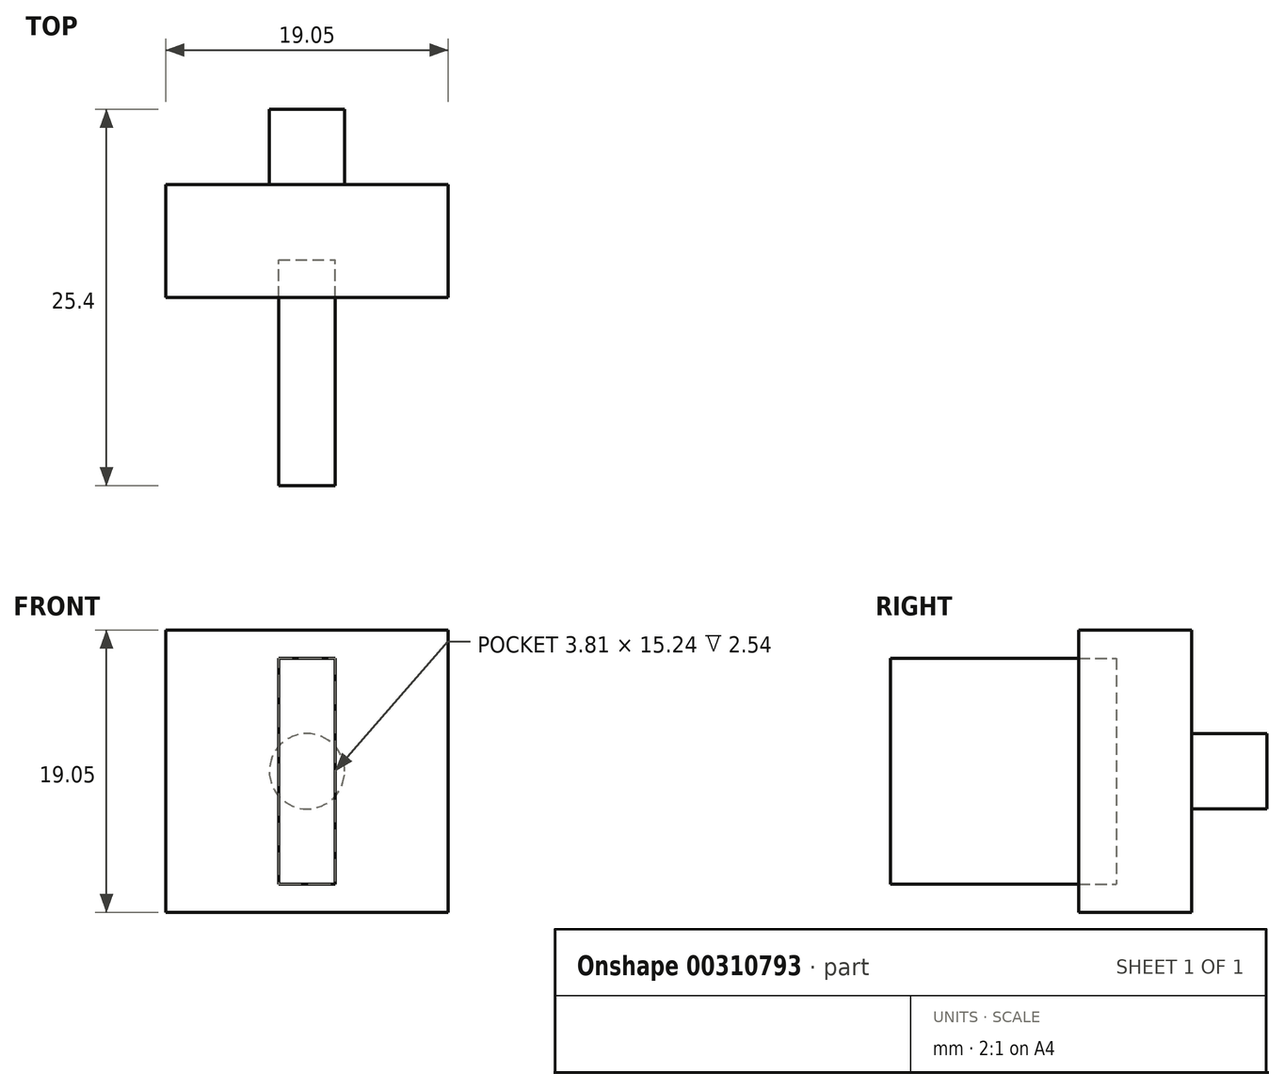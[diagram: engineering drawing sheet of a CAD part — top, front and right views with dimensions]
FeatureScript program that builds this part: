
annotation { "Feature Type Name" : "Feature", "Feature Type Description" : "" }
export const myFeature = defineFeature(function(context is Context, id is Id, definition is map)
    precondition{}
    {
        {
            var Q0;
            Q0=qCreatedBy(makeId("Front.planeOp"),FACE);
            var sketch = newSketch(context, id + "F0", { "sketchPlane" : qUnion([Q0])});
            skLineSegment(sketch, "E0", {"start": v(-7.62, 0) * mm, "end": v(11.43, 0) * mm});
            skLineSegment(sketch, "E1", {"start": v(11.43, 0) * mm, "end": v(11.43, 19.05) * mm});
            skLineSegment(sketch, "E2", {"start": v(11.43, 19.05) * mm, "end": v(-7.62, 19.05) * mm});
            skLineSegment(sketch, "E3", {"start": v(-7.62, 19.05) * mm, "end": v(-7.62, 0) * mm});
            skSolve(sketch);
        }
        {
            var Q0;
            Q0=makeQuery(id+"F0.imprint","IMPRINT",FACE,{"disambiguationData":[TD([[makeQuery(id+"F0.imprint","IMPRINT",EDGE,{"derivedFrom":sQuery(id+"F0.wireOp",EDGE,"E0")}),1.0]])]});
            extrude(context, id + "F1", {"entities" : qUnion([Q0]), "depth" : 7.62 * mm});
        }
        {
            var Q0;
            Q0=makeQuery(id+"F1.opExtrude","CAP_FACE",FACE,{"disambiguationData":[OSD([sQuery(id+"F0.wireOp",EDGE,"E0"),sQuery(id+"F0.wireOp",EDGE,"E1"),sQuery(id+"F0.wireOp",EDGE,"E2"),sQuery(id+"F0.wireOp",EDGE,"E3")])],"isStart":false});
            var sketch = newSketch(context, id + "F2", { "sketchPlane" : qUnion([Q0])});
            skLineSegment(sketch, "E4", {"start": v(0, 1.9) * mm, "end": v(3.8, 1.9) * mm});
            skLineSegment(sketch, "E5", {"start": v(3.8, 1.9) * mm, "end": v(3.8, 17.14) * mm});
            skLineSegment(sketch, "E6", {"start": v(3.8, 17.14) * mm, "end": v(0, 17.14) * mm});
            skLineSegment(sketch, "E7", {"start": v(0, 17.14) * mm, "end": v(0, 1.9) * mm});
            skSolve(sketch);
        }
        {
            var Q0;
            Q0=makeQuery(id+"F2.imprint","IMPRINT",FACE,{"disambiguationData":[TD([[makeQuery(id+"F2.imprint","IMPRINT",EDGE,{"derivedFrom":sQuery(id+"F2.wireOp",EDGE,"cbMtKTGd-g65i-xnvt-AXoW-RrOancOfgppl")}),1.0]])]});
            var Q1;
            Q1=makeQuery(id+"F2.imprint","IMPRINT",FACE,{"disambiguationData":[TD([[makeQuery(id+"F2.imprint","IMPRINT",EDGE,{"derivedFrom":sQuery(id+"F2.wireOp",EDGE,"E4")}),1.0]])]});
            extrude(context, id + "F3", {"entities" : qUnion([Q0, Q1]), "operationType" : NewBodyOperationType.REMOVE, "oppositeDirection" : true, "depth" : 2.54 * mm});
        }
        {
            var Q0;
            Q0=makeQuery(id+"F1.opExtrude","CAP_FACE",FACE,{"disambiguationData":[OSD([sQuery(id+"F0.wireOp",EDGE,"E0"),sQuery(id+"F0.wireOp",EDGE,"E1"),sQuery(id+"F0.wireOp",EDGE,"E2"),sQuery(id+"F0.wireOp",EDGE,"E3")])],"isStart":true});
            var sketch = newSketch(context, id + "F4", { "sketchPlane" : qUnion([Q0])});
            skPoint(sketch, "E8.centerSnap0", {"position": v(-11.43, 9.53) * mm});
            skCircle(sketch, "E9", {"center": v(-1.9, 9.53) * mm, "radius": 2.54 * mm});
            skPoint(sketch, "E9.centerSnap0", {"position": v(-1.9, 19.05) * mm});
            skPoint(sketch, "E9.centerSnap1", {"position": v(7.62, 9.53) * mm});
            skSolve(sketch);
        }
        {
            var Q0;
            Q0=makeQuery(id+"F4.imprint","IMPRINT",FACE,{"disambiguationData":[TD([[makeQuery(id+"F4.imprint","IMPRINT",EDGE,{"derivedFrom":sQuery(id+"F4.wireOp",EDGE,"E8")}),1.0]])]});
            var Q1;
            Q1=makeQuery(id+"F4.imprint","IMPRINT",FACE,{"disambiguationData":[TD([[makeQuery(id+"F4.imprint","IMPRINT",EDGE,{"derivedFrom":sQuery(id+"F4.wireOp",EDGE,"E9")}),1.0]])]});
            extrude(context, id + "F5", {"entities" : qUnion([Q0, Q1]), "operationType" : NewBodyOperationType.ADD, "depth" : 5.08 * mm});
        }
        {
            var Q0;
            Q0=makeQuery(id+"F3.boolean.opBoolean","COPY",FACE,{"derivedFrom":makeQuery(id+"F3.opExtrude","CAP_FACE",FACE,{"disambiguationData":[OSD([sQuery(id+"F2.wireOp",EDGE,"cbMtKTGd-g65i-xnvt-AXoW-RrOancOfgppl"),sQuery(id+"F2.wireOp",EDGE,"NMXBmVgW-MpaY-MJWR-DT77-MaYLcQVVOFlb"),sQuery(id+"F2.wireOp",EDGE,"Pu10IA7c-zYZb-xNST-tOOe-hBLO1BOZIXoM"),sQuery(id+"F2.wireOp",EDGE,"BYTWxHmh-r4Pu-ORZl-Lw5X-mh59dGRY3zhL")])],"isStart":false})});
            var Q1;
            Q1=makeQuery(id+"F3.boolean.opBoolean","COPY",FACE,{"derivedFrom":makeQuery(id+"F3.opExtrude","CAP_FACE",FACE,{"disambiguationData":[OSD([sQuery(id+"F2.wireOp",EDGE,"E4"),sQuery(id+"F2.wireOp",EDGE,"E5"),sQuery(id+"F2.wireOp",EDGE,"E6"),sQuery(id+"F2.wireOp",EDGE,"E7")])],"isStart":false})});
            extrude(context, id + "F6", {"entities" : qUnion([Q0, Q1]), "depth" : 15.24 * mm});
        }
    });
